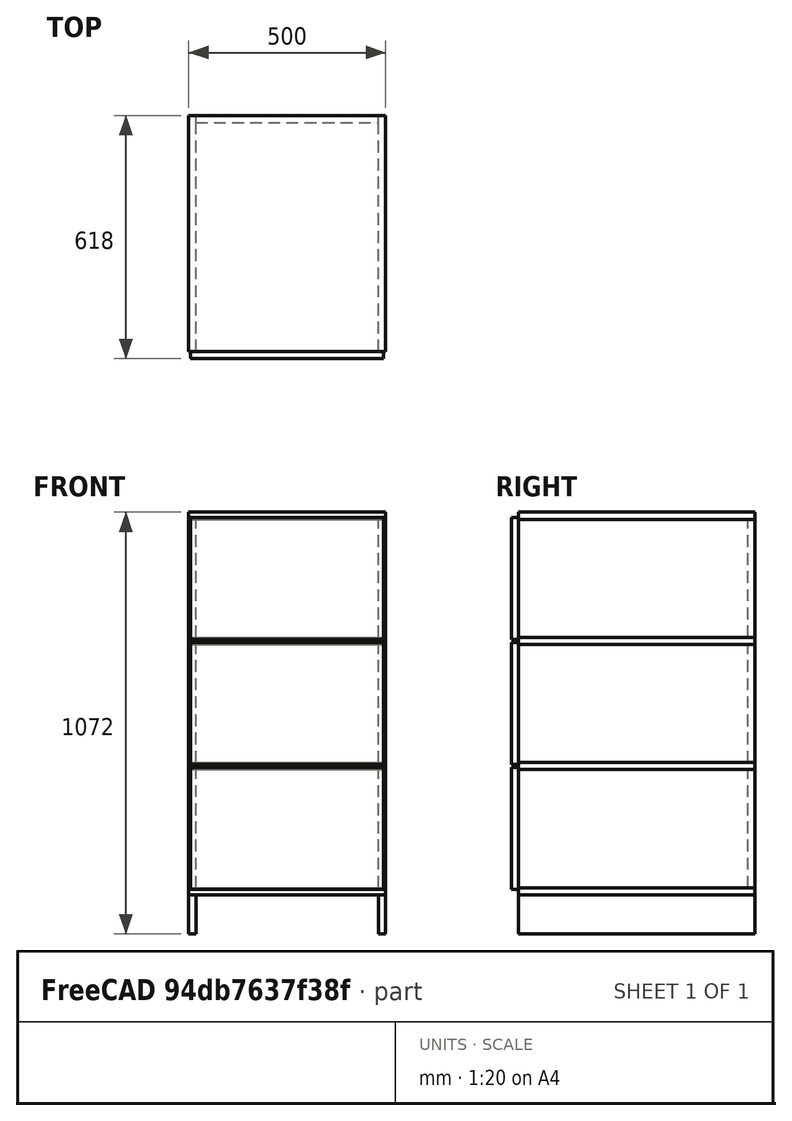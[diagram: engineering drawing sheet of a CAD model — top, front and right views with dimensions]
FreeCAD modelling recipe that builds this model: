
FCSTD DOCUMENT  (FreeCAD 1.1R20260325 (Git shallow))
Label: Test002_edgeband
License: All rights reserved
LicenseURL: http://en.wikipedia.org/wiki/All_rights_reserved
objects: Part::Box×18, App::DocumentObjectGroup×7, Spreadsheet::Sheet×1, TechDraw::DrawSVGTemplate×1, TechDraw::DrawViewSpreadsheet×1, TechDraw::DrawPage×1
note: 18 computed .brp shape members not serialized (recipe doc carries the construction recipe); baked Part::Feature solids carry a one-line shape summary decoded from their .brp

FEATURE [Part::Box] Box006  label="Foot L"
  AttacherType = Attacher::AttachEngine3D
  Height = 100
  Length = 18
  Width = 600
FEATURE [Part::Box] Box007  label="Side L1"
  AttacherType = Attacher::AttachEngine3D
  Height = 300
  Length = 18
  Placement = pos=(0,0,118) rot=(0,0,1;0rad)
  Width = 600
FEATURE [Part::Box] Box008  label="Side L2"
  AttacherType = Attacher::AttachEngine3D
  Height = 300
  Length = 18
  Placement = pos=(0,0,436) rot=(0,0,1;0rad)
  Width = 600
FEATURE [Part::Box] Box009  label="Side L3"
  AttacherType = Attacher::AttachEngine3D
  Height = 300
  Length = 18
  Placement = pos=(0,0,754) rot=(0,0,1;0rad)
  Width = 600
FEATURE [Part::Box] Box010  label="Foot R"
  AttacherType = Attacher::AttachEngine3D
  Height = 100
  Length = 18
  Placement = pos=(482,0,0) rot=(0,0,1;0rad)
  Width = 600
FEATURE [Part::Box] Box011  label="Side R1"
  AttacherType = Attacher::AttachEngine3D
  Height = 300
  Length = 18
  Placement = pos=(482,0,118) rot=(0,0,1;0rad)
  Width = 600
FEATURE [Part::Box] Box012  label="Side R2"
  AttacherType = Attacher::AttachEngine3D
  Height = 300
  Length = 18
  Placement = pos=(482,0,436) rot=(0,0,1;0rad)
  Width = 600
FEATURE [Part::Box] Box013  label="Side R3"
  AttacherType = Attacher::AttachEngine3D
  Height = 300
  Length = 18
  Placement = pos=(482,0,754) rot=(0,0,1;0rad)
  Width = 600
FEATURE [Part::Box] Box018  label="Back 1"
  AttacherType = Attacher::AttachEngine3D
  Height = 300
  Length = 464
  Placement = pos=(18,582,118) rot=(0,0,1;0rad)
  Width = 18
FEATURE [Part::Box] Box019  label="Back 2"
  AttacherType = Attacher::AttachEngine3D
  Height = 300
  Length = 464
  Placement = pos=(18,582,436) rot=(0,0,1;0rad)
  Width = 18
FEATURE [Part::Box] Box020  label="Back 3"
  AttacherType = Attacher::AttachEngine3D
  Height = 300
  Length = 464
  Placement = pos=(18,582,754) rot=(0,0,1;0rad)
  Width = 18
FEATURE [Part::Box] Box023  label="Top 1"
  AttacherType = Attacher::AttachEngine3D
  Height = 18
  Length = 500
  Placement = pos=(0,0,100) rot=(0,0,1;0rad)
  Width = 600
FEATURE [Part::Box] Box024  label="Top 2"
  AttacherType = Attacher::AttachEngine3D
  Height = 18
  Length = 500
  Placement = pos=(0,0,418) rot=(0,0,1;0rad)
  Width = 600
FEATURE [Part::Box] Box025  label="Top 3"
  AttacherType = Attacher::AttachEngine3D
  Height = 18
  Length = 500
  Placement = pos=(0,0,736) rot=(0,0,1;0rad)
  Width = 600
FEATURE [Part::Box] Box026  label="Top 4"
  AttacherType = Attacher::AttachEngine3D
  Height = 18
  Length = 500
  Placement = pos=(0,0,1054) rot=(0,0,1;0rad)
  Width = 600
FEATURE [Part::Box] Box027  label="Front 1"
  AttacherType = Attacher::AttachEngine3D
  Height = 310
  Length = 490
  Placement = pos=(5,-18,113) rot=(0,0,1;0rad)
  Width = 18
FEATURE [Part::Box] Box028  label="Front 2"
  AttacherType = Attacher::AttachEngine3D
  Height = 310
  Length = 490
  Placement = pos=(5,-18,431) rot=(0,0,1;0rad)
  Width = 18
FEATURE [Part::Box] Box029  label="Front 3"
  AttacherType = Attacher::AttachEngine3D
  Height = 310
  Length = 490
  Placement = pos=(5,-18,749) rot=(0,0,1;0rad)
  Width = 18
FEATURE [App::DocumentObjectGroup] Group006  label="Front"
  Group = -> [Box027,Box028,Box029]
FEATURE [App::DocumentObjectGroup] Group005  label="Top"
  Group = -> [Box023,Box024,Box025,Box026]
FEATURE [App::DocumentObjectGroup] Group004  label="Back"
  Group = -> [Box018,Box019,Box020]
FEATURE [App::DocumentObjectGroup] Group003  label="Side"
  Group = -> [Box007,Box008,Box009,Box011,Box012,Box013]
FEATURE [App::DocumentObjectGroup] Group007  label="Foot"
  Group = -> [Box006,Box010]
FEATURE [App::DocumentObjectGroup] Group002  label="White"
  Group = -> [Group003,Group004,Group005,Group006,Group007]
FEATURE [App::DocumentObjectGroup] Group001  label="Parts"
  Group = -> [Group002]
FEATURE [Spreadsheet::Sheet] toCut
  cells = A1='Name; B1='Dimensions; E1='Thickness; F1='Quantity; G1='m^2; A2='Foot L; B2='100 mm; C2='x; D2='600 mm; E2='18 mm; F2=1; G2='0.06; A3=5; B3=6; D3=1; E3=2; F3=3; G3=4; A4='edge; F4='edge; G4='edge; A5='600 mm; F5='100 mm; G5='100 mm; A6='black; F6='black; G6='black; A8='Name; B8='Dimensions; E8='Thickness; F8='Quantity; G8='m^2; A9='Side L1; B9='300 mm; C9='x; D9='600 mm; E9='18 mm; F9=1; G9='0.18; A10=5; B10=6; D10=1; E10=2; F10=3; G10=4; F11='edge; G11='edge; F12='300 mm; G12='300 mm; F13='black; G13='black; A15='Name; B15='Dimensions; E15='Thickness; F15='Quantity; G15='m^2; A16='Side L2; B16='300 mm; C16='x; D16='600 mm; E16='18 mm; F16=1; G16='0.18; A17=5; B17=6; D17=1; E17=2; F17=3; G17=4; F18='edge; G18='edge; F19='300 mm; G19='300 mm; F20='black; G20='black; A22='Name; B22='Dimensions; E22='Thickness; F22='Quantity; G22='m^2; A23='Side L3; B23='300 mm; C23='x; D23='600 mm; E23='18 mm; F23=1; G23='0.18; A24=5; B24=6; D24=1; E24=2; F24=3; G24=4; F25='edge; G25='edge; F26='300 mm; G26='300 mm; F27='black; G27='black; A29='Name; B29='Dimensions; E29='Thickness; F29='Quantity; G29='m^2; A30='Foot R; B30='100 mm; C30='x; D30='600 mm; E30='18 mm; F30=1; G30='0.06; A31=5; B31=6; D31=1; E31=2; F31=3; G31=4; A32='edge; F32='edge; G32='edge; A33='600 mm; F33='100 mm; G33='100 mm; A34='black; F34='black; G34='black; A36='Name; B36='Dimensions; E36='Thickness; F36='Quantity; G36='m^2; A37='Side R1; B37='300 mm; C37='x; D37='600 mm; E37='18 mm; F37=1; G37='0.18; A38=5; B38=6; D38=1; E38=2; F38=3; G38=4; F39='edge; G39='edge; F40='300 mm; G40='300 mm; F41='black; G41='black; A43='Name; B43='Dimensions; E43='Thickness; F43='Quantity; G43='m^2; A44='Side R2; B44='300 mm; C44='x; D44='600 mm; E44='18 mm; F44=1; G44='0.18; A45=5; B45=6; D45=1; E45=2; F45=3; G45=4; F46='edge; G46='edge; F47='300 mm; G47='300 mm; F48='black; G48='black; A50='Name; B50='Dimensions; E50='Thickness; F50='Quantity; G50='m^2; A51='Side R3; B51='300 mm; C51='x; D51='600 mm; E51='18 mm; F51=1; G51='0.18; A52=5; B52=6; D52=1; E52=2; F52=3; G52=4; F53='edge; G53='edge; F54='300 mm; G54='300 mm; F55='black; G55='black; A57='Name; B57='Dimensions; +260 more cells
FEATURE [TechDraw::DrawSVGTemplate] Template
  Height = 297
  Orientation = 0
  Template = <path>
  Width = 210
FEATURE [TechDraw::DrawViewSpreadsheet] Sheet
  CellEnd = G124
  CellStart = A1
  Font = DejaVu Sans
  LineWidth = 0.1
  LockPosition = false
  Rotation = 0
  ScaleType = 2
  Source = -> toCut
  Symbol = <blob: 159619 chars omitted>
  TextSize = 13
  X = 105
  Y = 148
FEATURE [TechDraw::DrawPage] toPrint
  KeepUpdated = true
  NextBalloonIndex = 1
  ProjectionType = 0
  Template = -> Template
  Views = -> [Sheet]
note: 1 file-system path scrubbed to <path> (originals preserved in the JSON sidecar)
